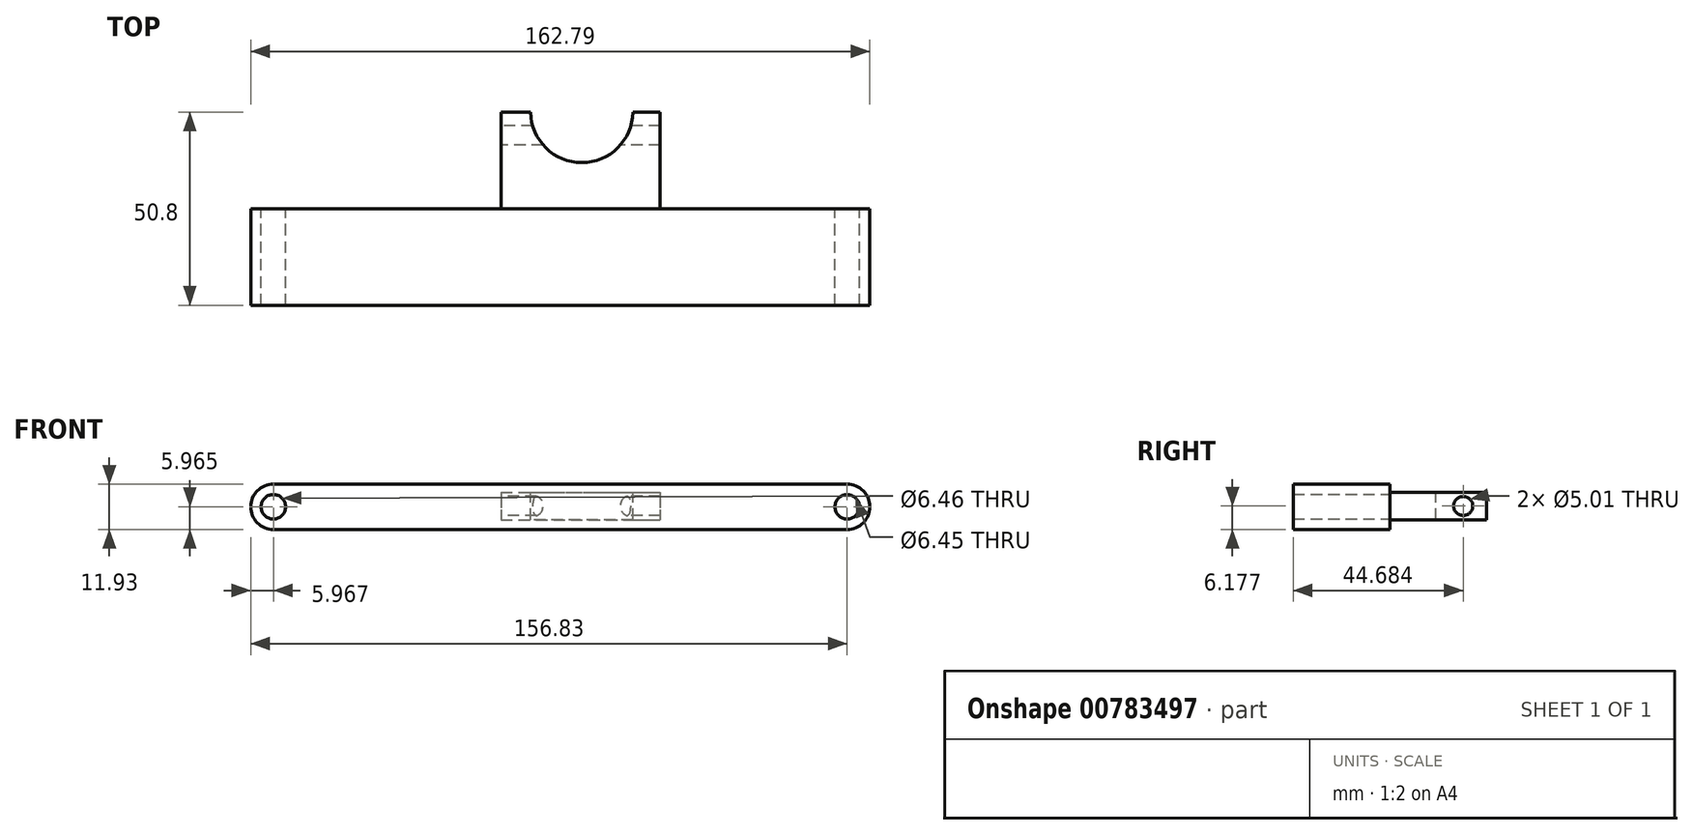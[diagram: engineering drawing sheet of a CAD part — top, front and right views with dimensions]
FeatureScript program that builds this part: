
annotation { "Feature Type Name" : "Feature", "Feature Type Description" : "" }
export const myFeature = defineFeature(function(context is Context, id is Id, definition is map)
    precondition{}
    {
        {
            var Q0;
            Q0=qCreatedBy(makeId("Front.planeOp"),FACE);
            var sketch = newSketch(context, id + "F0", { "sketchPlane" : qUnion([Q0])});
            skLineSegment(sketch, "E0.bottom", {"start": v(-75.8, 11.93) * mm, "end": v(75.07, 11.93) * mm});
            skLineSegment(sketch, "E0.top", {"start": v(-75.8, 0) * mm, "end": v(75.07, 0) * mm});
            skLineSegment(sketch, "E0.left", {"start": v(-75.8, 11.93) * mm, "end": v(-75.8, 0) * mm});
            skLineSegment(sketch, "E0.right", {"start": v(75.07, 11.93) * mm, "end": v(75.07, 0) * mm});
            skArc(sketch, "E1", {"start": v(-75.8, 11.93) * mm, "mid": v(-81.76, 5.96) * mm, "end": v(-75.8, 0) * mm});
            skArc(sketch, "E2", {"start": v(75.07, 0) * mm, "mid": v(81.03, 5.96) * mm, "end": v(75.07, 11.93) * mm});
            skCircle(sketch, "E3", {"center": v(-75.8, 5.96) * mm, "radius": 3.23 * mm});
            skCircle(sketch, "E4", {"center": v(75.07, 5.96) * mm, "radius": 3.23 * mm});
            skSolve(sketch);
        }
        {
            var Q0;
            Q0 = qSketchRegion(id + "F0", true);
            extrude(context, id + "F1", {"entities" : qUnion([Q0]), "depth" : 25.4 * mm, "offsetDistance" : 25.4 * mm});
        }
        {
            var Q0;
            Q0=qCreatedBy(makeId("Front.planeOp"),FACE);
            var sketch = newSketch(context, id + "F2", { "sketchPlane" : qUnion([Q0])});
            skLineSegment(sketch, "E5.bottom", {"start": v(-15.93, 9.75) * mm, "end": v(25.89, 9.75) * mm});
            skLineSegment(sketch, "E5.top", {"start": v(-15.93, 2.54) * mm, "end": v(25.89, 2.54) * mm});
            skLineSegment(sketch, "E5.left", {"start": v(-15.93, 9.75) * mm, "end": v(-15.93, 2.54) * mm});
            skLineSegment(sketch, "E5.right", {"start": v(25.89, 9.75) * mm, "end": v(25.89, 2.54) * mm});
            skSolve(sketch);
        }
        {
            var Q0;
            Q0 = qSketchRegion(id + "F2", true);
            extrude(context, id + "F3", {"entities" : qUnion([Q0]), "operationType" : NewBodyOperationType.ADD, "oppositeDirection" : true, "depth" : 25.4 * mm, "offsetDistance" : 25.4 * mm});
        }
        {
            var Q0;
            Q0=makeQuery(id+"F3.opExtrude","SWEPT_FACE",FACE,{"disambiguationData":[OSD([sQuery(id+"F2.wireOp",EDGE,"E5.bottom")])]});
            var sketch = newSketch(context, id + "F4", { "sketchPlane" : qUnion([Q0])});
            skArc(sketch, "E6", {"start": v(-8.15, 25.4) * mm, "mid": v(5.3, 12.12) * mm, "end": v(18.73, 25.4) * mm});
            skSolve(sketch);
        }
        {
            var Q0;
            Q0 = qSketchRegion(id + "F4", true);
            var Q1;
            {var subQ0=sQuery(id+"F4.wireOp",EDGE,"E6");Q1=makeQuery(id+"F4.imprint","IMPRINT",FACE,{"disambiguationData":[TD([[makeQuery(id+"F4.imprint","IMPRINT",EDGE,{"derivedFrom":subQ0}),1.0]])]});}
            extrude(context, id + "F5", {"entities" : qUnion([Q0, Q1]), "operationType" : NewBodyOperationType.REMOVE, "oppositeDirection" : true, "depth" : 7.62 * mm, "offsetDistance" : 25.4 * mm});
        }
        {
            var Q0;
            Q0=makeQuery(id+"F3.opExtrude","SWEPT_FACE",FACE,{"disambiguationData":[OSD([sQuery(id+"F2.wireOp",EDGE,"E5.left")])]});
            var sketch = newSketch(context, id + "F6", { "sketchPlane" : qUnion([Q0])});
            skCircle(sketch, "E7", {"center": v(-19.28, 6.18) * mm, "radius": 2.5 * mm});
            skSolve(sketch);
        }
        {
            var Q0;
            Q0 = qSketchRegion(id + "F6", true);
            extrude(context, id + "F7", {"entities" : qUnion([Q0]), "operationType" : NewBodyOperationType.REMOVE, "oppositeDirection" : true, "depth" : 45.97 * mm, "offsetDistance" : 25.4 * mm});
        }
    });
